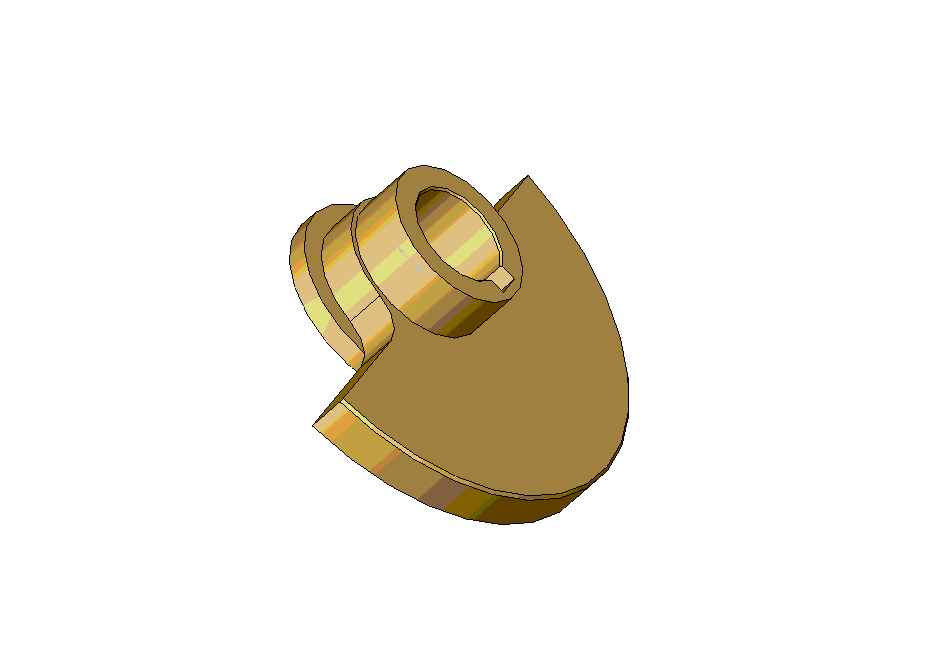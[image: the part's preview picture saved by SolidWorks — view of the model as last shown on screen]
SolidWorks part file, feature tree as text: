
SOLIDWORKS PART (.sldprt)
format: sldprt  version: not decoded by parser v0  size: 260,608 bytes
history: native  units: mm
features: chamfer x3, plane x2, sketch x2, cut_extrude x2, material x1, pattern_circular x1 + 1 further entry (+12 scaffold rows collapsed)
feature tree (24):
  scaffold x12  (default folders/planes/origin — collapsed)
  material  "Material <not specified>"
  "6. gegengewicht vorn<1>@6. gegengewicht vorn"
  plane  "Plane1"  Offset=0mm
  sketch  "Sketch1"  dims[D1=1.5mm D2=1.5mm D3=6.5mm]
  cut_extrude  "Cut-Extrude1"  [1 undecoded]
  plane  "Plane2"  Offset=0mm
  sketch  "Sketch2"  dims[D2=~0.931324mm D1=7.5mm]
  cut_extrude  "Cut-Extrude2"  Depth=1mm
  pattern_circular  "CirPattern1"  Count=12 Angle=360deg
  chamfer  "Chamfer1"  Distance=0.2mm Angle=45deg
  chamfer  "Chamfer2"  Distance=0.2mm Angle=45deg
  chamfer  "Chamfer3"  Distance=0.3mm Angle=45deg
decode coverage: 7 of 8 modeling features carry decoded parameters; 1 rows unclassified (native names shown)
note: ~ marks probable driven/reference dimensions
note: 1 parameter value undecoded
note: suppression state not decoded; provenance and decode notes live in map.json
